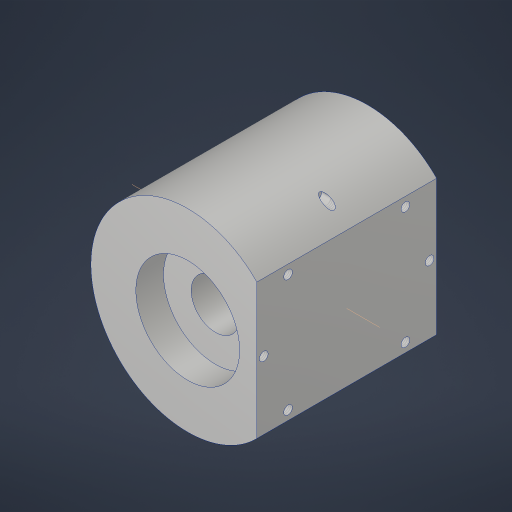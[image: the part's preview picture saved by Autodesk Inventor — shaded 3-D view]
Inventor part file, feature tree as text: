
AUTODESK INVENTOR PART (.ipt)
format: ipt  version: 2023.4 (Build 274418000, 418)  size: 255,488 bytes
history: native  units: in
note: dims shown in document units (in); Inventor stores cm internally (conversion verified against a paired STEP export)
features: sketch x5, extrude x4, projected_geometry x3, hole x1, other x1, pattern_circular x1
ambient origin geometry x8: Origin, YZ Plane, XZ Plane, XY Plane, X Axis, Y Axis, Z Axis, Center Point
bodies: Solid1 (feature_tree)
feature tree (15):
  extrude  "Extrusion1"  Depth=4.5in
  extrude  "Extrusion2"  Depth=0.25in
  extrude  "Extrusion3"  Depth=0.8358in
  hole  "Hole1"  [1 undecoded]
  other  "Work Axis1"
  pattern_circular  "Circular Pattern1"  [2 undecoded]
  extrude  "Extrusion4"  Depth=1.875in
  sketch  "Sketch1"  dims[d0=0.875in d2=4.5in]
  sketch  "Sketch3"  dims[d3=3.5in d4=0.25in]
  sketch  "Sketch4"  dims[d5=1.4142in d6=0.8358in]
  sketch  "Sketch5"  dims[d7=1.25in d8=3.25in d9=0.0in]
  sketch  "Sketch6"  dims[d10=1.875in d11=0.5in d12=0.0in d13=1.875in d14=0.5in d15=0.0in d16=3.0in d17=0.156in d18=0.38in d19=0.385in d20=0.25in d21=0.5635in d22=0.536in d23=0.0in d24=3.1496in d25=360.0deg d27=0.5in d28=1.0in d29=0.0in]
  projected_geometry  "Project Cut Edges1"
  projected_geometry  "Project Cut Edges2"
  projected_geometry  "Project Cut Edges3"
note: 3 required parameter values undecoded (feature->parameter linkage not recoverable at this tier; creation-order binding heuristic only, values carry confidence <= 0.55)
